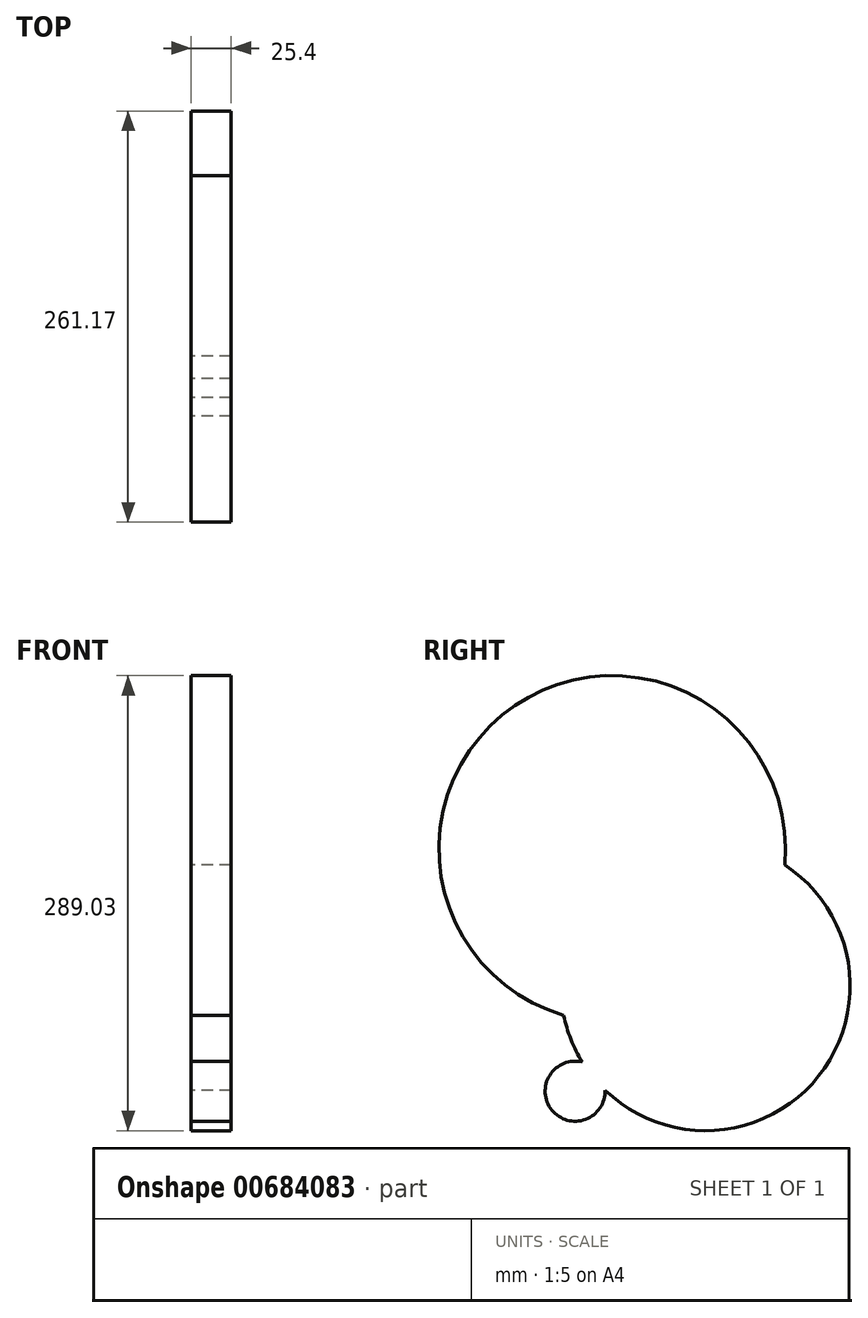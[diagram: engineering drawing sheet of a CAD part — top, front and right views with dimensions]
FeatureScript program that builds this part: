
annotation { "Feature Type Name" : "Feature", "Feature Type Description" : "" }
export const myFeature = defineFeature(function(context is Context, id is Id, definition is map)
    precondition{}
    {
        {
            var Q0;
            Q0=qCreatedBy(makeId("Right.planeOp"),FACE);
            var sketch = newSketch(context, id + "F0", { "sketchPlane" : qUnion([Q0])});
            skCircle(sketch, "E0", {"center": v(-6.5, -29.9) * mm, "radius": 19.06 * mm});
            skCircle(sketch, "E1", {"center": v(76.26, 37) * mm, "radius": 91.93 * mm});
            skCircle(sketch, "E2", {"center": v(17.07, 124.04) * mm, "radius": 110.04 * mm});
            skLineSegment(sketch, "E3", {"start": v(-21.65, -11.13) * mm, "end": v(-41.18, -36.65) * mm});
            skLineSegment(sketch, "E4", {"start": v(-41.18, -36.65) * mm, "end": v(-41.18, -51.18) * mm});
            skSolve(sketch);
        }
        {
            var Q0;
            {var subQ0=sQuery(id+"F0.wireOp",EDGE,"E2");var subQ1=sQuery(id+"F0.wireOp",EDGE,"E1");var subQ2=makeQuery(id+"F0.imprint","INTERSECT",VERTEX,{"disambiguationData":[OD(0.0)],"derivedFrom":[subQ1,subQ0]});Q0=makeQuery(id+"F0.imprint","IMPRINT",FACE,{"disambiguationData":[TD([[makeQuery(id+"F0.imprint","IMPRINT",EDGE,{"disambiguationData":[TD([[subQ2,1.0]])],"derivedFrom":subQ1}),-1.0]])]});}
            var Q1;
            {var subQ0=sQuery(id+"F0.wireOp",EDGE,"E2");var subQ1=sQuery(id+"F0.wireOp",EDGE,"E1");var subQ2=makeQuery(id+"F0.imprint","INTERSECT",VERTEX,{"disambiguationData":[OD(0.0)],"derivedFrom":[subQ1,subQ0]});Q1=makeQuery(id+"F0.imprint","IMPRINT",FACE,{"disambiguationData":[TD([[makeQuery(id+"F0.imprint","IMPRINT",EDGE,{"disambiguationData":[TD([[subQ2,1.0]])],"derivedFrom":subQ1}),1.0]])]});}
            var Q2;
            {var subQ0=sQuery(id+"F0.wireOp",EDGE,"E1");var subQ1=sQuery(id+"F0.wireOp",EDGE,"E0");var subQ2=makeQuery(id+"F0.imprint","INTERSECT",VERTEX,{"disambiguationData":[OD(0.0)],"derivedFrom":[subQ1,subQ0]});Q2=makeQuery(id+"F0.imprint","IMPRINT",FACE,{"disambiguationData":[TD([[makeQuery(id+"F0.imprint","IMPRINT",EDGE,{"disambiguationData":[TD([[subQ2,1.0]])],"derivedFrom":subQ1}),1.0]])]});}
            var Q3;
            {var subQ0=sQuery(id+"F0.wireOp",EDGE,"E1");var subQ1=sQuery(id+"F0.wireOp",EDGE,"E0");var subQ2=makeQuery(id+"F0.imprint","INTERSECT",VERTEX,{"disambiguationData":[OD(0.0)],"derivedFrom":[subQ1,subQ0]});Q3=makeQuery(id+"F0.imprint","IMPRINT",FACE,{"disambiguationData":[TD([[makeQuery(id+"F0.imprint","IMPRINT",EDGE,{"disambiguationData":[TD([[subQ2,-1.0]])],"derivedFrom":subQ1}),1.0]])]});}
            var Q4;
            {var subQ0=sQuery(id+"F0.wireOp",EDGE,"E1");var subQ1=sQuery(id+"F0.wireOp",EDGE,"E0");var subQ2=makeQuery(id+"F0.imprint","INTERSECT",VERTEX,{"disambiguationData":[OD(0.0)],"derivedFrom":[subQ1,subQ0]});Q4=makeQuery(id+"F0.imprint","IMPRINT",FACE,{"disambiguationData":[TD([[makeQuery(id+"F0.imprint","IMPRINT",EDGE,{"disambiguationData":[TD([[subQ2,1.0]])],"derivedFrom":subQ1}),-1.0]])]});}
            extrude(context, id + "F1", {"entities" : qUnion([Q0, Q1, Q2, Q3, Q4]), "depth" : 25.4 * mm, "offsetDistance" : 25.4 * mm});
        }
    });
